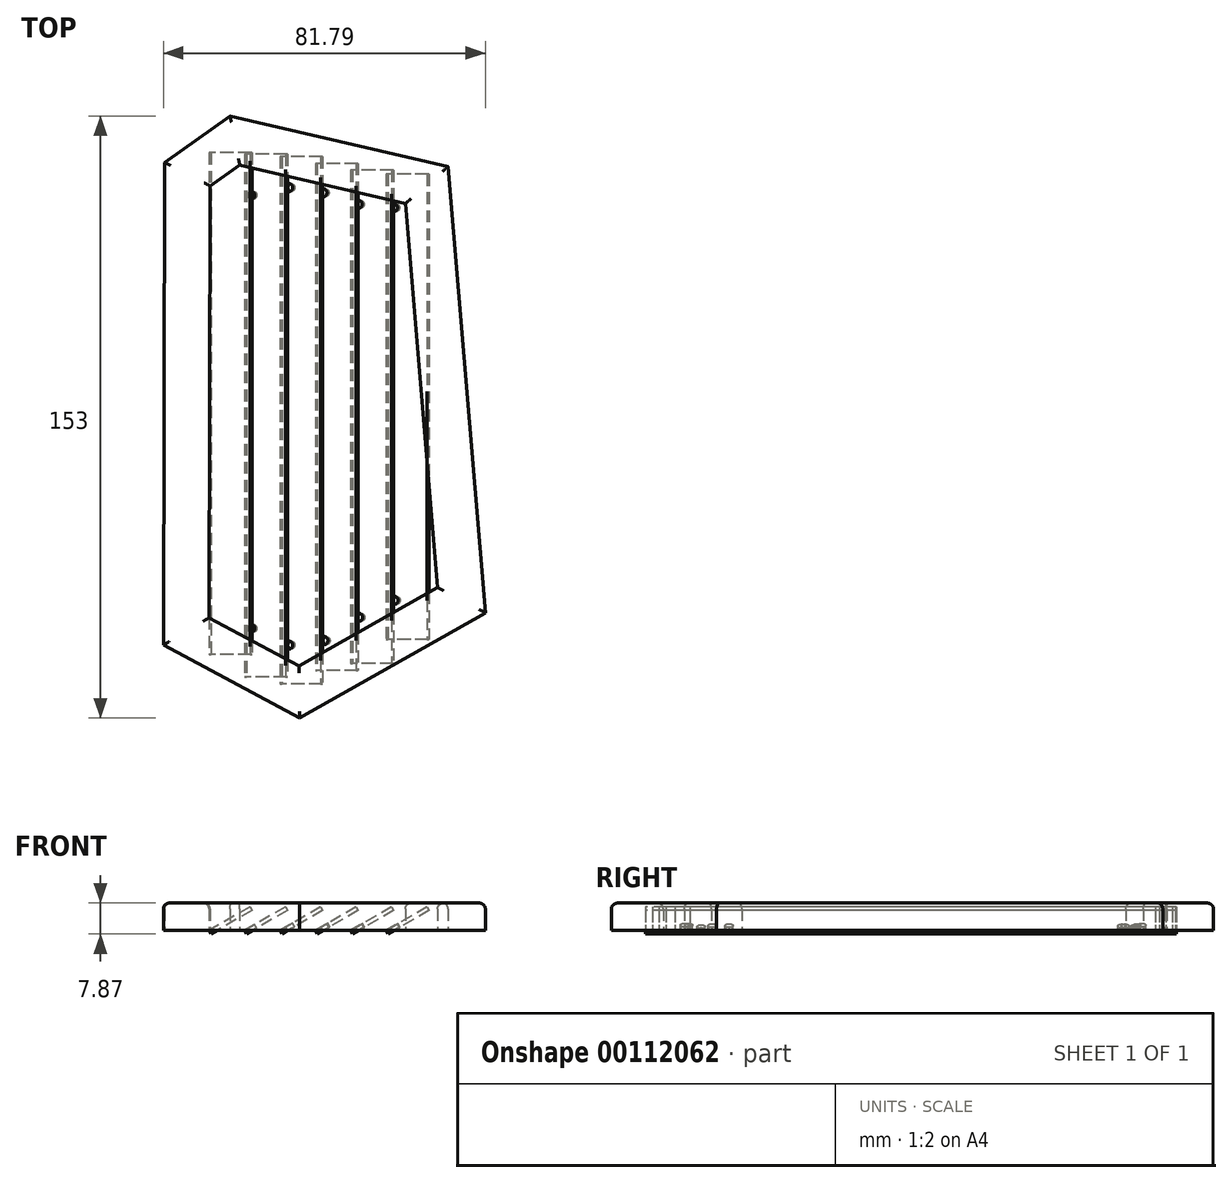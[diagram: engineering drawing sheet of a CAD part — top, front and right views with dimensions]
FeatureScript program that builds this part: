
annotation { "Feature Type Name" : "Feature", "Feature Type Description" : "" }
export const myFeature = defineFeature(function(context is Context, id is Id, definition is map)
    precondition{}
    {
        {
            var Q0;
            Q0=qCreatedBy(makeId("Top.planeOp"),FACE);
            var sketch = newSketch(context, id + "F0", { "sketchPlane" : qUnion([Q0])});
            skLineSegment(sketch, "E0", {"start": v(-11.27, 5.4) * mm, "end": v(-11.6, -117.21) * mm});
            skLineSegment(sketch, "E1", {"start": v(-11.6, -117.21) * mm, "end": v(23.01, -135.77) * mm});
            skLineSegment(sketch, "E2", {"start": v(70.2, -109.02) * mm, "end": v(60.73, 4.3) * mm});
            skLineSegment(sketch, "E3", {"start": v(60.73, 4.3) * mm, "end": v(5.34, 17.23) * mm});
            skLineSegment(sketch, "E4", {"start": v(0, -110.3) * mm, "end": v(0.3, -0.58) * mm});
            skLineSegment(sketch, "E5", {"start": v(0.3, -0.58) * mm, "end": v(7.8, 4.77) * mm});
            skLineSegment(sketch, "E6", {"start": v(7.8, 4.77) * mm, "end": v(49.9, -5.05) * mm});
            skLineSegment(sketch, "E7", {"start": v(49.9, -5.05) * mm, "end": v(58.05, -102.6) * mm});
            skLineSegment(sketch, "E8", {"start": v(58.05, -102.6) * mm, "end": v(22.86, -122.56) * mm});
            skLineSegment(sketch, "E9", {"start": v(22.86, -122.56) * mm, "end": v(0, -110.3) * mm});
            skLineSegment(sketch, "E10", {"start": v(-11.27, 5.4) * mm, "end": v(5.34, 17.23) * mm});
            skLineSegment(sketch, "E11", {"start": v(23.01, -135.77) * mm, "end": v(70.2, -109.02) * mm});
            skSolve(sketch);
        }
        {
            var Q0;
            Q0=qCreatedBy(makeId("Top.planeOp"),FACE);
            var sketch = newSketch(context, id + "F1", { "sketchPlane" : qUnion([Q0])});
            skLineSegment(sketch, "E12.bottom", {"start": v(0, 7.85) * mm, "end": v(1, 7.85) * mm});
            skLineSegment(sketch, "E12.top", {"start": v(0, -119.56) * mm, "end": v(1, -119.56) * mm});
            skLineSegment(sketch, "E12.left", {"start": v(0, 7.85) * mm, "end": v(0, -119.56) * mm});
            skLineSegment(sketch, "E12.right", {"start": v(1, 7.85) * mm, "end": v(1, -119.56) * mm});
            skLineSegment(sketch, "E13.bottom", {"start": v(9, 7.5) * mm, "end": v(10, 7.5) * mm});
            skLineSegment(sketch, "E13.top", {"start": v(9, -125.34) * mm, "end": v(10, -125.34) * mm});
            skLineSegment(sketch, "E13.left", {"start": v(9, 7.5) * mm, "end": v(9, -125.34) * mm});
            skLineSegment(sketch, "E13.right", {"start": v(10, 7.5) * mm, "end": v(10, -125.34) * mm});
            skLineSegment(sketch, "E14.bottom", {"start": v(18, 6.83) * mm, "end": v(19, 6.83) * mm});
            skLineSegment(sketch, "E14.top", {"start": v(18, -127.04) * mm, "end": v(19, -127.04) * mm});
            skLineSegment(sketch, "E14.left", {"start": v(18, 6.83) * mm, "end": v(18, -127.04) * mm});
            skLineSegment(sketch, "E14.right", {"start": v(19, 6.83) * mm, "end": v(19, -127.04) * mm});
            skLineSegment(sketch, "E15.bottom", {"start": v(36, 3.43) * mm, "end": v(37, 3.43) * mm});
            skLineSegment(sketch, "E15.top", {"start": v(36, -121.94) * mm, "end": v(37, -121.94) * mm});
            skLineSegment(sketch, "E15.left", {"start": v(36, 3.43) * mm, "end": v(36, -121.94) * mm});
            skLineSegment(sketch, "E15.right", {"start": v(37, 3.43) * mm, "end": v(37, -121.94) * mm});
            skLineSegment(sketch, "E16.bottom", {"start": v(45, 2.4) * mm, "end": v(46, 2.4) * mm});
            skLineSegment(sketch, "E16.top", {"start": v(45, -115.83) * mm, "end": v(46, -115.83) * mm});
            skLineSegment(sketch, "E16.left", {"start": v(45, 2.4) * mm, "end": v(45, -115.83) * mm});
            skLineSegment(sketch, "E16.right", {"start": v(46, 2.4) * mm, "end": v(46, -115.83) * mm});
            skLineSegment(sketch, "E17.bottom", {"start": v(27, 5.13) * mm, "end": v(28, 5.13) * mm});
            skLineSegment(sketch, "E17.top", {"start": v(27, -123.64) * mm, "end": v(28, -123.64) * mm});
            skLineSegment(sketch, "E17.left", {"start": v(27, 5.13) * mm, "end": v(27, -123.64) * mm});
            skLineSegment(sketch, "E17.right", {"start": v(28, 5.13) * mm, "end": v(28, -123.64) * mm});
            skLineSegment(sketch, "E18", {"start": v(0, -14.95) * mm, "end": v(50.43, -14.95) * mm, "construction": true});
            skSolve(sketch);
        }
        {
            var Q0;
            Q0 = qSketchRegion(id + "F1", true);
            extrude(context, id + "F2", {"entities" : qUnion([Q0]), "depth" : 12 * mm});
        }
        {
            var Q0;
            Q0=makeQuery(id+"F2.opExtrude","SWEPT_BODY",BODY,{"disambiguationData":[OSD([sQuery(id+"F1.wireOp",EDGE,"E12.bottom"),sQuery(id+"F1.wireOp",EDGE,"E12.top"),sQuery(id+"F1.wireOp",EDGE,"E12.left"),sQuery(id+"F1.wireOp",EDGE,"E12.right")])]});
            var Q1;
            Q1=makeQuery(id+"F2.opExtrude","CAP_EDGE",EDGE,{"disambiguationData":[OSD([sQuery(id+"F1.wireOp",EDGE,"E12.left")])],"isStart":true});
            transform(context, id + "F3", {"entities" : qUnion([Q0]), "transformType" : TransformType.ROTATION, "transformAxis" : qUnion([Q1]), "angle" : 60 * degree, "oppositeDirection" : true, "makeCopy" : false});
        }
        {
            var Q0;
            Q0=makeQuery(id+"F2.opExtrude","SWEPT_BODY",BODY,{"disambiguationData":[OSD([sQuery(id+"F1.wireOp",EDGE,"E13.bottom"),sQuery(id+"F1.wireOp",EDGE,"E13.top"),sQuery(id+"F1.wireOp",EDGE,"E13.left"),sQuery(id+"F1.wireOp",EDGE,"E13.right")])]});
            var Q1;
            Q1=makeQuery(id+"F2.opExtrude","CAP_EDGE",EDGE,{"disambiguationData":[OSD([sQuery(id+"F1.wireOp",EDGE,"E13.left")])],"isStart":true});
            transform(context, id + "F4", {"entities" : qUnion([Q0]), "transformType" : TransformType.ROTATION, "transformAxis" : qUnion([Q1]), "angle" : 60 * degree, "oppositeDirection" : true, "makeCopy" : false});
        }
        {
            var Q0;
            Q0=makeQuery(id+"F2.opExtrude","SWEPT_BODY",BODY,{"disambiguationData":[OSD([sQuery(id+"F1.wireOp",EDGE,"E14.bottom"),sQuery(id+"F1.wireOp",EDGE,"E14.top"),sQuery(id+"F1.wireOp",EDGE,"E14.left"),sQuery(id+"F1.wireOp",EDGE,"E14.right")])]});
            var Q1;
            Q1=makeQuery(id+"F2.opExtrude","CAP_EDGE",EDGE,{"disambiguationData":[OSD([sQuery(id+"F1.wireOp",EDGE,"E14.left")])],"isStart":true});
            transform(context, id + "F5", {"entities" : qUnion([Q0]), "transformType" : TransformType.ROTATION, "transformAxis" : qUnion([Q1]), "angle" : 60 * degree, "oppositeDirection" : true, "makeCopy" : false});
        }
        {
            var Q0;
            Q0=makeQuery(id+"F2.opExtrude","SWEPT_BODY",BODY,{"disambiguationData":[OSD([sQuery(id+"F1.wireOp",EDGE,"E17.bottom"),sQuery(id+"F1.wireOp",EDGE,"E17.top"),sQuery(id+"F1.wireOp",EDGE,"E17.left"),sQuery(id+"F1.wireOp",EDGE,"E17.right")])]});
            var Q1;
            Q1=makeQuery(id+"F2.opExtrude","CAP_EDGE",EDGE,{"disambiguationData":[OSD([sQuery(id+"F1.wireOp",EDGE,"E17.left")])],"isStart":true});
            transform(context, id + "F6", {"entities" : qUnion([Q0]), "transformType" : TransformType.ROTATION, "transformAxis" : qUnion([Q1]), "angle" : 60 * degree, "oppositeDirection" : true, "makeCopy" : false});
        }
        {
            var Q0;
            Q0=makeQuery(id+"F2.opExtrude","SWEPT_BODY",BODY,{"disambiguationData":[OSD([sQuery(id+"F1.wireOp",EDGE,"E15.bottom"),sQuery(id+"F1.wireOp",EDGE,"E15.top"),sQuery(id+"F1.wireOp",EDGE,"E15.left"),sQuery(id+"F1.wireOp",EDGE,"E15.right")])]});
            var Q1;
            Q1=makeQuery(id+"F2.opExtrude","CAP_EDGE",EDGE,{"disambiguationData":[OSD([sQuery(id+"F1.wireOp",EDGE,"E15.left")])],"isStart":true});
            transform(context, id + "F7", {"entities" : qUnion([Q0]), "transformType" : TransformType.ROTATION, "transformAxis" : qUnion([Q1]), "angle" : 60 * degree, "oppositeDirection" : true, "makeCopy" : false});
        }
        {
            var Q0;
            Q0=makeQuery(id+"F2.opExtrude","SWEPT_BODY",BODY,{"disambiguationData":[OSD([sQuery(id+"F1.wireOp",EDGE,"E16.bottom"),sQuery(id+"F1.wireOp",EDGE,"E16.top"),sQuery(id+"F1.wireOp",EDGE,"E16.left"),sQuery(id+"F1.wireOp",EDGE,"E16.right")])]});
            var Q1;
            Q1=makeQuery(id+"F2.opExtrude","CAP_EDGE",EDGE,{"disambiguationData":[OSD([sQuery(id+"F1.wireOp",EDGE,"E16.left")])],"isStart":true});
            transform(context, id + "F8", {"entities" : qUnion([Q0]), "transformType" : TransformType.ROTATION, "transformAxis" : qUnion([Q1]), "angle" : 60 * degree, "oppositeDirection" : true, "makeCopy" : false});
        }
        {
            var Q0;
            Q0=makeQuery(id+"F2.opExtrude","SWEPT_FACE",FACE,{"disambiguationData":[OSD([sQuery(id+"F1.wireOp",EDGE,"E13.left")])]});
            var sketch = newSketch(context, id + "F9", { "sketchPlane" : qUnion([Q0])});
            skPoint(sketch, "E19", {"position": v(9.8, -112.96) * mm});
            skPoint(sketch, "E20", {"position": v(9.8, -2.94) * mm});
            skSolve(sketch);
        }
        {
            var Q0;
            Q0=sQuery(id+"F9.wireOp",VERTEX,"E19");
            var Q1;
            Q1=sQuery(id+"F9.wireOp",VERTEX,"E20");
            var Q2;
            Q2=makeQuery(id+"F2.opExtrude","SWEPT_BODY",BODY,{"disambiguationData":[OSD([sQuery(id+"F1.wireOp",EDGE,"E13.bottom"),sQuery(id+"F1.wireOp",EDGE,"E13.top"),sQuery(id+"F1.wireOp",EDGE,"E13.left"),sQuery(id+"F1.wireOp",EDGE,"E13.right")])]});
            hole(context, id + "F10", {"style" : HoleStyle.SIMPLE, "endStyle" : HoleEndStyle.THROUGH, "holeDiameter" : 2 * mm, "locations" : qUnion([Q0, Q1]), "scope" : qUnion([Q2]), "isTappedThrough" : true});
        }
        {
            var Q0;
            Q0=makeQuery(id+"F2.opExtrude","SWEPT_FACE",FACE,{"disambiguationData":[OSD([sQuery(id+"F1.wireOp",EDGE,"E14.left")])]});
            var sketch = newSketch(context, id + "F11", { "sketchPlane" : qUnion([Q0])});
            skPoint(sketch, "E21", {"position": v(18.32, -1) * mm});
            skPoint(sketch, "E22", {"position": v(18.32, -117.22) * mm});
            skSolve(sketch);
        }
        {
            var Q0;
            Q0=sQuery(id+"F11.wireOp",VERTEX,"E22");
            var Q1;
            Q1=sQuery(id+"F11.wireOp",VERTEX,"E21");
            var Q2;
            Q2=makeQuery(id+"F2.opExtrude","SWEPT_BODY",BODY,{"disambiguationData":[OSD([sQuery(id+"F1.wireOp",EDGE,"E14.bottom"),sQuery(id+"F1.wireOp",EDGE,"E14.top"),sQuery(id+"F1.wireOp",EDGE,"E14.left"),sQuery(id+"F1.wireOp",EDGE,"E14.right")])]});
            hole(context, id + "F12", {"style" : HoleStyle.SIMPLE, "endStyle" : HoleEndStyle.THROUGH, "holeDiameter" : 2 * mm, "locations" : qUnion([Q0, Q1]), "scope" : qUnion([Q2]), "isTappedThrough" : true});
        }
        {
            var Q0;
            Q0=makeQuery(id+"F2.opExtrude","SWEPT_FACE",FACE,{"disambiguationData":[OSD([sQuery(id+"F1.wireOp",EDGE,"E17.left")])]});
            var sketch = newSketch(context, id + "F13", { "sketchPlane" : qUnion([Q0])});
            skPoint(sketch, "E23", {"position": v(25.78, -2.3) * mm});
            skPoint(sketch, "E24", {"position": v(26.07, -116.09) * mm});
            skSolve(sketch);
        }
        {
            var Q0;
            Q0=sQuery(id+"F13.wireOp",VERTEX,"E23");
            var Q1;
            Q1=sQuery(id+"F13.wireOp",VERTEX,"E24");
            var Q2;
            Q2=makeQuery(id+"F2.opExtrude","SWEPT_BODY",BODY,{"disambiguationData":[OSD([sQuery(id+"F1.wireOp",EDGE,"E17.bottom"),sQuery(id+"F1.wireOp",EDGE,"E17.top"),sQuery(id+"F1.wireOp",EDGE,"E17.left"),sQuery(id+"F1.wireOp",EDGE,"E17.right")])]});
            hole(context, id + "F14", {"style" : HoleStyle.SIMPLE, "endStyle" : HoleEndStyle.THROUGH, "holeDiameter" : 2 * mm, "locations" : qUnion([Q0, Q1]), "scope" : qUnion([Q2]), "isTappedThrough" : true});
        }
        {
            var Q0;
            Q0=makeQuery(id+"F2.opExtrude","SWEPT_FACE",FACE,{"disambiguationData":[OSD([sQuery(id+"F1.wireOp",EDGE,"E15.left")])]});
            var sketch = newSketch(context, id + "F15", { "sketchPlane" : qUnion([Q0])});
            skPoint(sketch, "E25", {"position": v(33.5, -5.24) * mm});
            skPoint(sketch, "E26", {"position": v(33.67, -110.18) * mm});
            skSolve(sketch);
        }
        {
            var Q0;
            Q0=sQuery(id+"F15.wireOp",VERTEX,"E26");
            var Q1;
            Q1=sQuery(id+"F15.wireOp",VERTEX,"E25");
            var Q2;
            Q2=makeQuery(id+"F2.opExtrude","SWEPT_BODY",BODY,{"disambiguationData":[OSD([sQuery(id+"F1.wireOp",EDGE,"E15.bottom"),sQuery(id+"F1.wireOp",EDGE,"E15.top"),sQuery(id+"F1.wireOp",EDGE,"E15.left"),sQuery(id+"F1.wireOp",EDGE,"E15.right")])]});
            hole(context, id + "F16", {"style" : HoleStyle.SIMPLE, "endStyle" : HoleEndStyle.THROUGH, "holeDiameter" : 2 * mm, "locations" : qUnion([Q0, Q1]), "scope" : qUnion([Q2]), "isTappedThrough" : true});
        }
        {
            var Q0;
            Q0=makeQuery(id+"F2.opExtrude","SWEPT_FACE",FACE,{"disambiguationData":[OSD([sQuery(id+"F1.wireOp",EDGE,"E16.left")])]});
            var sketch = newSketch(context, id + "F17", { "sketchPlane" : qUnion([Q0])});
            skPoint(sketch, "E27", {"position": v(41.46, -105.87) * mm});
            skPoint(sketch, "E28", {"position": v(41.29, -6.1) * mm});
            skSolve(sketch);
        }
        {
            var Q0;
            Q0=sQuery(id+"F17.wireOp",VERTEX,"E28");
            var Q1;
            Q1=sQuery(id+"F17.wireOp",VERTEX,"E27");
            var Q2;
            Q2=makeQuery(id+"F2.opExtrude","SWEPT_BODY",BODY,{"disambiguationData":[OSD([sQuery(id+"F1.wireOp",EDGE,"E16.bottom"),sQuery(id+"F1.wireOp",EDGE,"E16.top"),sQuery(id+"F1.wireOp",EDGE,"E16.left"),sQuery(id+"F1.wireOp",EDGE,"E16.right")])]});
            hole(context, id + "F18", {"style" : HoleStyle.SIMPLE, "endStyle" : HoleEndStyle.THROUGH, "holeDiameter" : 2 * mm, "locations" : qUnion([Q0, Q1]), "scope" : qUnion([Q2]), "isTappedThrough" : true});
        }
        {
            var Q0;
            Q0 = qSketchRegion(id + "F0", true);
            extrude(context, id + "F19", {"entities" : qUnion([Q0]), "depth" : 7 * mm});
        }
        {
            var Q0;
            Q0=makeQuery(id+"F19.opExtrude","CAP_FACE",FACE,{"disambiguationData":[OSD([sQuery(id+"F0.wireOp",EDGE,"E0"),sQuery(id+"F0.wireOp",EDGE,"E1"),sQuery(id+"F0.wireOp",EDGE,"E2"),sQuery(id+"F0.wireOp",EDGE,"E3"),sQuery(id+"F0.wireOp",EDGE,"E4"),sQuery(id+"F0.wireOp",EDGE,"E5"),sQuery(id+"F0.wireOp",EDGE,"E6"),sQuery(id+"F0.wireOp",EDGE,"E7"),sQuery(id+"F0.wireOp",EDGE,"E8"),sQuery(id+"F0.wireOp",EDGE,"E9"),sQuery(id+"F0.wireOp",EDGE,"E10"),sQuery(id+"F0.wireOp",EDGE,"E11")])],"isStart":false});
            fillet(context, id + "F20", {"entities" : qUnion([Q0]), "radius" : 1.5 * mm, "tangentPropagation" : true, "allowEdgeOverflow" : false});
        }
    });
